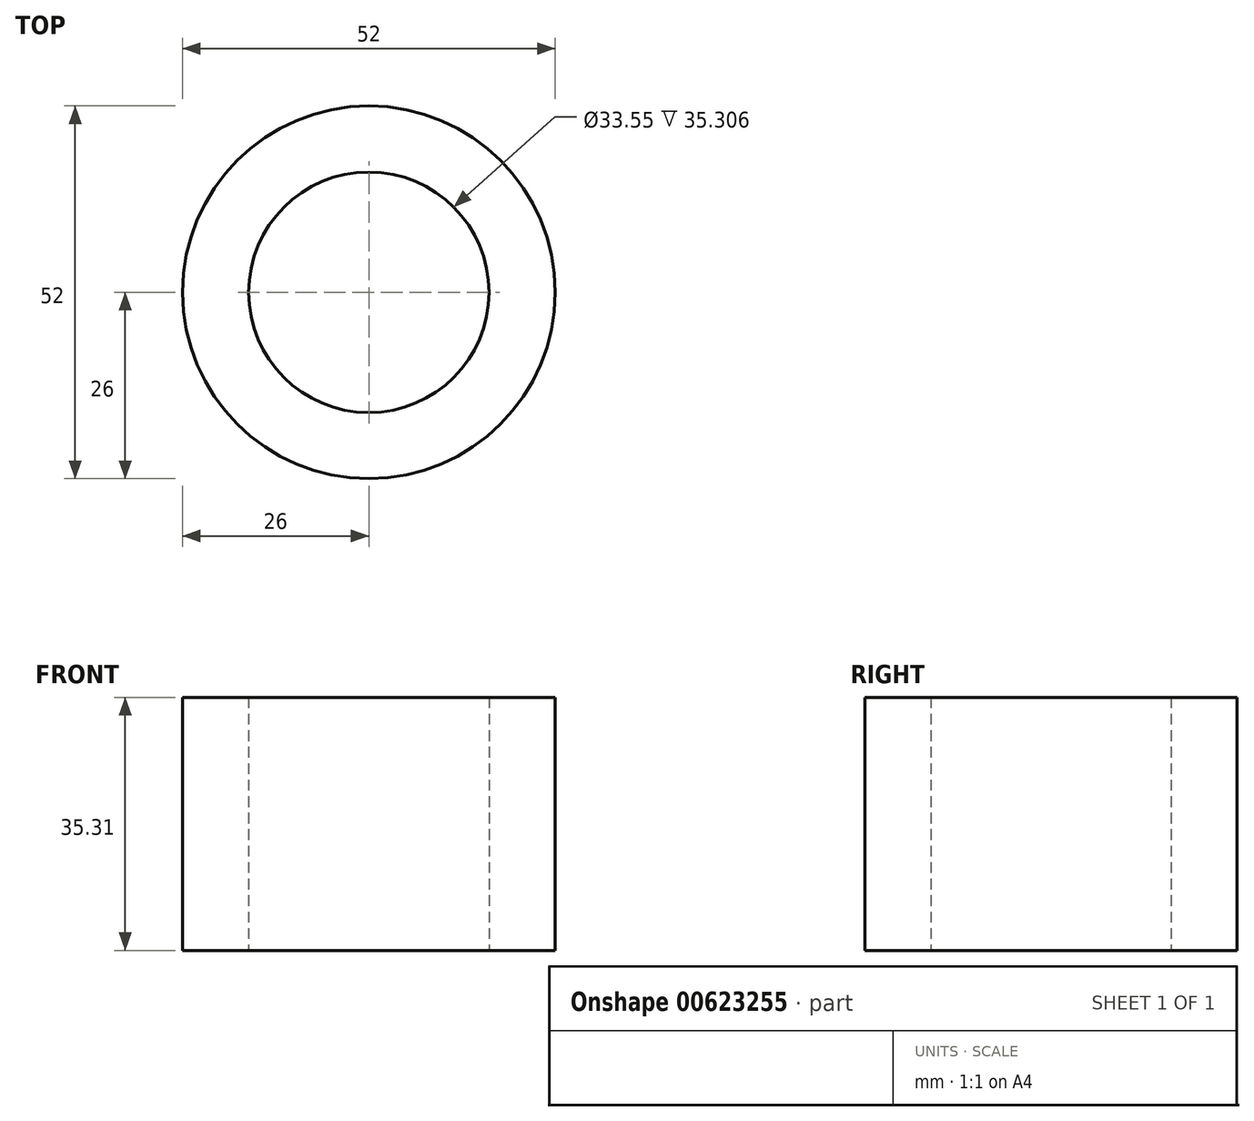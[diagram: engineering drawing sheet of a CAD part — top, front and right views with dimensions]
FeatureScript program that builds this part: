
annotation { "Feature Type Name" : "Feature", "Feature Type Description" : "" }
export const myFeature = defineFeature(function(context is Context, id is Id, definition is map)
    precondition{}
    {
        {
            var Q0;
            Q0=qCreatedBy(makeId("Top.planeOp"),FACE);
            var sketch = newSketch(context, id + "F0", { "sketchPlane" : qUnion([Q0])});
            skCircle(sketch, "E0", {"center": v(0, 0) * mm, "radius": 26 * mm});
            skSolve(sketch);
        }
        {
            var Q0;
            Q0 = qSketchRegion(id + "F0", true);
            extrude(context, id + "F1", {"entities" : qUnion([Q0]), "depth" : 35.3 * mm, "offsetDistance" : 25.4 * mm});
        }
        {
            var Q0;
            Q0=qCreatedBy(makeId("Top.planeOp"),FACE);
            var sketch = newSketch(context, id + "F2", { "sketchPlane" : qUnion([Q0])});
            skCircle(sketch, "E1", {"center": v(0, 0) * mm, "radius": 16.77 * mm});
            skSolve(sketch);
        }
        {
            var Q0;
            Q0 = qSketchRegion(id + "F2", true);
            var Q1;
            Q1=makeQuery(id+"F1.opExtrude","CAP_FACE",FACE,{"disambiguationData":[OSD([sQuery(id+"F0.wireOp",EDGE,"E0")])],"isStart":false});
            extrude(context, id + "F3", {"entities" : qUnion([Q0, Q1]), "operationType" : NewBodyOperationType.REMOVE, "depth" : 105.16 * mm, "offsetDistance" : 25.4 * mm});
        }
    });
